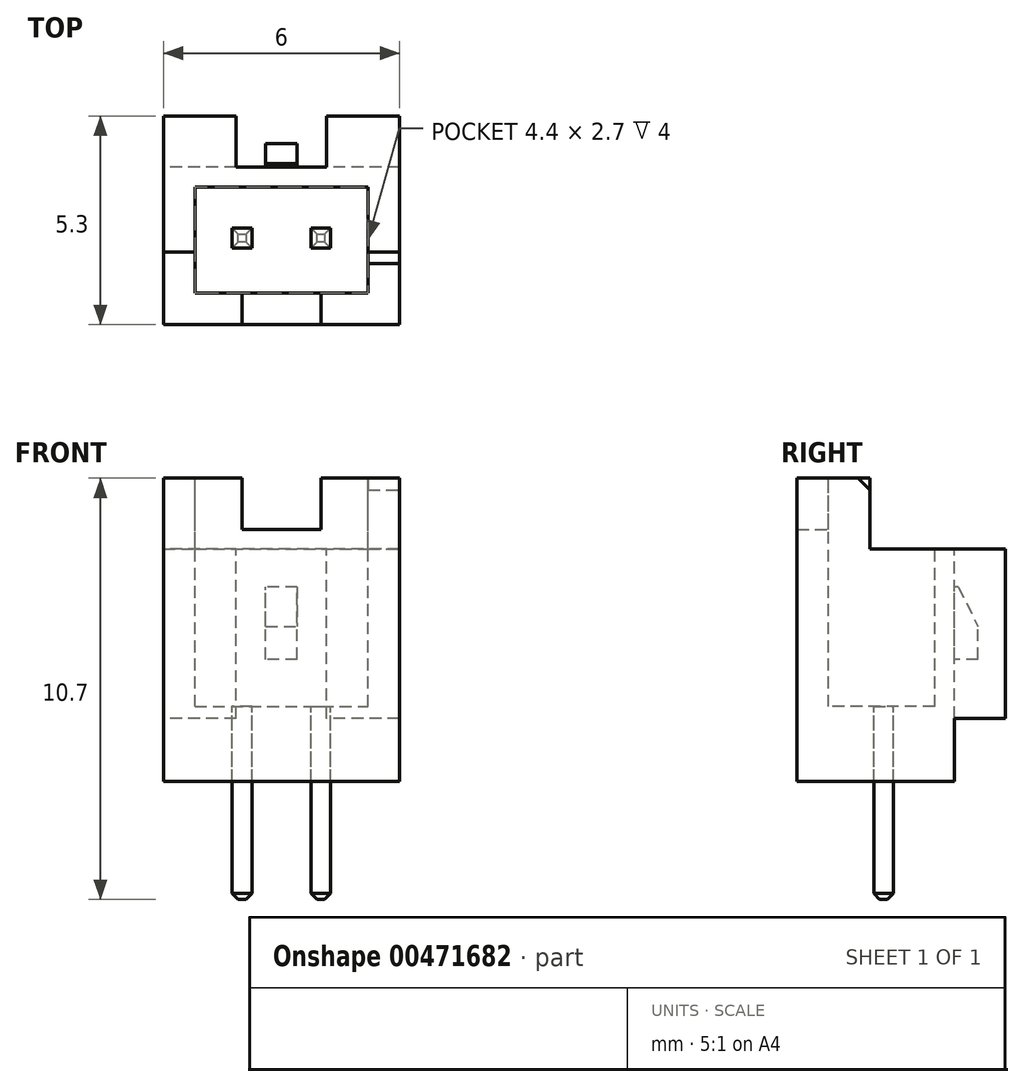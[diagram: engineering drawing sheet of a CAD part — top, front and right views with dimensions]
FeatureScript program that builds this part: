
annotation { "Feature Type Name" : "Feature", "Feature Type Description" : "" }
export const myFeature = defineFeature(function(context is Context, id is Id, definition is map)
    precondition{}
    {
        {
            var Q0;
            Q0=qCreatedBy(makeId("Top.planeOp"),FACE);
            var sketch = newSketch(context, id + "F0", { "sketchPlane" : qUnion([Q0])});
            skLineSegment(sketch, "E0.bottom", {"start": v(0.25, 0.25) * mm, "end": v(-0.25, 0.25) * mm});
            skLineSegment(sketch, "E0.top", {"start": v(0.25, -0.25) * mm, "end": v(-0.25, -0.25) * mm});
            skLineSegment(sketch, "E0.left", {"start": v(0.25, 0.25) * mm, "end": v(0.25, -0.25) * mm});
            skLineSegment(sketch, "E0.right", {"start": v(-0.25, 0.25) * mm, "end": v(-0.25, -0.25) * mm});
            skPoint(sketch, "E0.middle", {"position": v(0, 0) * mm});
            skLineSegment(sketch, "E1.bottom", {"start": v(-2.25, 0.25) * mm, "end": v(-1.75, 0.25) * mm});
            skLineSegment(sketch, "E1.top", {"start": v(-2.25, -0.25) * mm, "end": v(-1.75, -0.25) * mm});
            skLineSegment(sketch, "E1.left", {"start": v(-2.25, 0.25) * mm, "end": v(-2.25, -0.25) * mm});
            skLineSegment(sketch, "E1.right", {"start": v(-1.75, 0.25) * mm, "end": v(-1.75, -0.25) * mm});
            skPoint(sketch, "E1.middle", {"position": v(-2, 0) * mm});
            skSolve(sketch);
        }
        {
            var Q0;
            Q0=makeQuery(id+"F0.imprint","IMPRINT",FACE,{"disambiguationData":[TD([[makeQuery(id+"F0.imprint","IMPRINT",EDGE,{"derivedFrom":sQuery(id+"F0.wireOp",EDGE,"E1.bottom")}),-1.0]])]});
            var Q1;
            Q1=makeQuery(id+"F0.imprint","IMPRINT",FACE,{"disambiguationData":[TD([[makeQuery(id+"F0.imprint","IMPRINT",EDGE,{"derivedFrom":sQuery(id+"F0.wireOp",EDGE,"E0.bottom")}),1.0]])]});
            extrude(context, id + "F1", {"entities" : qUnion([Q0, Q1]), "oppositeDirection" : true, "depth" : 3 * mm, "hasSecondDirection" : true, "secondDirectionOppositeDirection" : false, "secondDirectionDepth" : 4 * mm});
        }
        {
            var Q0;
            Q0=qCreatedBy(makeId("Top.planeOp"),FACE);
            var sketch = newSketch(context, id + "F2", { "sketchPlane" : qUnion([Q0])});
            skLineSegment(sketch, "E2.bottom", {"start": v(2, -2.2) * mm, "end": v(-4, -2.2) * mm});
            skLineSegment(sketch, "E2.top", {"start": v(2, 3.1) * mm, "end": v(-4, 3.1) * mm});
            skLineSegment(sketch, "E2.left", {"start": v(2, -2.2) * mm, "end": v(2, 3.1) * mm});
            skLineSegment(sketch, "E2.right", {"start": v(-4, -2.2) * mm, "end": v(-4, 3.1) * mm});
            skSolve(sketch);
        }
        {
            var Q0;
            Q0=makeQuery(id+"F2.imprint","IMPRINT",FACE,{"disambiguationData":[TD([[makeQuery(id+"F2.imprint","IMPRINT",EDGE,{"derivedFrom":sQuery(id+"F2.wireOp",EDGE,"E2.bottom")}),-1.0]])]});
            extrude(context, id + "F3", {"entities" : qUnion([Q0]), "depth" : 7.7 * mm});
        }
        {
            var Q0;
            Q0=makeQuery(id+"F3.opExtrude","CAP_FACE",FACE,{"disambiguationData":[OSD([sQuery(id+"F2.wireOp",EDGE,"E2.bottom"),sQuery(id+"F2.wireOp",EDGE,"E2.top"),sQuery(id+"F2.wireOp",EDGE,"E2.left"),sQuery(id+"F2.wireOp",EDGE,"E2.right")])],"isStart":false});
            var sketch = newSketch(context, id + "F4", { "sketchPlane" : qUnion([Q0])});
            skLineSegment(sketch, "E3.bottom", {"start": v(-3.2, 1.3) * mm, "end": v(1.2, 1.3) * mm});
            skLineSegment(sketch, "E3.top", {"start": v(-3.2, -1.4) * mm, "end": v(1.2, -1.4) * mm});
            skLineSegment(sketch, "E3.left", {"start": v(-3.2, 1.3) * mm, "end": v(-3.2, -1.4) * mm});
            skLineSegment(sketch, "E3.right", {"start": v(1.2, 1.3) * mm, "end": v(1.2, -1.4) * mm});
            skSolve(sketch);
        }
        {
            var Q0;
            Q0=makeQuery(id+"F4.imprint","IMPRINT",FACE,{"disambiguationData":[TD([[makeQuery(id+"F4.imprint","IMPRINT",EDGE,{"derivedFrom":sQuery(id+"F4.wireOp",EDGE,"E3.bottom")}),-1.0]])]});
            extrude(context, id + "F5", {"entities" : qUnion([Q0]), "operationType" : NewBodyOperationType.REMOVE, "oppositeDirection" : true, "depth" : 5.8 * mm});
        }
        {
            var Q0;
            Q0=makeQuery(id+"F3.opExtrude","CAP_FACE",FACE,{"disambiguationData":[OSD([sQuery(id+"F2.wireOp",EDGE,"E2.bottom"),sQuery(id+"F2.wireOp",EDGE,"E2.top"),sQuery(id+"F2.wireOp",EDGE,"E2.left"),sQuery(id+"F2.wireOp",EDGE,"E2.right")])],"isStart":false});
            var sketch = newSketch(context, id + "F6", { "sketchPlane" : qUnion([Q0])});
            skLineSegment(sketch, "E4.bottom", {"start": v(-2, -2.2) * mm, "end": v(0, -2.2) * mm});
            skLineSegment(sketch, "E4.top", {"start": v(-2, -1.4) * mm, "end": v(0, -1.4) * mm});
            skLineSegment(sketch, "E4.left", {"start": v(-2, -2.2) * mm, "end": v(-2, -1.4) * mm});
            skLineSegment(sketch, "E4.right", {"start": v(0, -2.2) * mm, "end": v(0, -1.4) * mm});
            skLineSegment(sketch, "E5.bottom", {"start": v(-4, 3.1) * mm, "end": v(2, 3.1) * mm});
            skLineSegment(sketch, "E5.top", {"start": v(-4, -0.35) * mm, "end": v(2, -0.35) * mm});
            skLineSegment(sketch, "E5.left", {"start": v(-4, 3.1) * mm, "end": v(-4, -0.35) * mm});
            skLineSegment(sketch, "E5.right", {"start": v(2, 3.1) * mm, "end": v(2, -0.35) * mm});
            skSolve(sketch);
        }
        {
            var Q0;
            Q0=makeQuery(id+"F6.imprint","IMPRINT",FACE,{"disambiguationData":[TD([[makeQuery(id+"F6.imprint","IMPRINT",EDGE,{"derivedFrom":sQuery(id+"F6.wireOp",EDGE,"E4.bottom")}),-1.0]])]});
            extrude(context, id + "F7", {"entities" : qUnion([Q0]), "operationType" : NewBodyOperationType.REMOVE, "oppositeDirection" : true, "depth" : 1.3 * mm});
        }
        {
            var Q0;
            Q0=makeQuery(id+"F6.imprint","IMPRINT",FACE,{"disambiguationData":[TD([[makeQuery(id+"F6.imprint","IMPRINT",EDGE,{"derivedFrom":sQuery(id+"F6.wireOp",EDGE,"E5.bottom")}),1.0]])]});
            extrude(context, id + "F8", {"entities" : qUnion([Q0]), "operationType" : NewBodyOperationType.REMOVE, "oppositeDirection" : true, "depth" : 1.8 * mm});
        }
        {
            var Q0;
            Q0=makeQuery(id+"F8.boolean.opBoolean","COPY",FACE,{"derivedFrom":makeQuery(id+"F8.opExtrude","CAP_FACE",FACE,{"disambiguationData":[OSD([sQuery(id+"F4.wireOp",EDGE,"E3.bottom"),sQuery(id+"F4.wireOp",EDGE,"E3.left"),sQuery(id+"F4.wireOp",EDGE,"E3.right"),sQuery(id+"F6.wireOp",EDGE,"E5.bottom"),sQuery(id+"F6.wireOp",EDGE,"E5.top"),sQuery(id+"F6.wireOp",EDGE,"E5.left"),sQuery(id+"F6.wireOp",EDGE,"E5.right")])],"isStart":false})});
            var sketch = newSketch(context, id + "F9", { "sketchPlane" : qUnion([Q0])});
            skLineSegment(sketch, "E6.bottom", {"start": v(0.15, 3.1) * mm, "end": v(-2.15, 3.1) * mm});
            skLineSegment(sketch, "E6.top", {"start": v(0.15, 1.8) * mm, "end": v(-2.15, 1.8) * mm});
            skLineSegment(sketch, "E6.left", {"start": v(0.15, 3.1) * mm, "end": v(0.15, 1.8) * mm});
            skLineSegment(sketch, "E6.right", {"start": v(-2.15, 3.1) * mm, "end": v(-2.15, 1.8) * mm});
            skSolve(sketch);
        }
        {
            var Q0;
            Q0=makeQuery(id+"F9.imprint","IMPRINT",FACE,{"disambiguationData":[TD([[makeQuery(id+"F9.imprint","IMPRINT",EDGE,{"derivedFrom":sQuery(id+"F9.wireOp",EDGE,"E6.bottom")}),1.0]])]});
            extrude(context, id + "F10", {"entities" : qUnion([Q0]), "operationType" : NewBodyOperationType.REMOVE, "oppositeDirection" : true, "depth" : 25 * mm});
        }
        {
            var Q0;
            Q0=makeQuery(id+"F10.boolean.opBoolean","COPY",FACE,{"derivedFrom":makeQuery(id+"F10.opExtrude","SWEPT_FACE",FACE,{"disambiguationData":[OSD([sQuery(id+"F9.wireOp",EDGE,"E6.top")])]})});
            var sketch = newSketch(context, id + "F11", { "sketchPlane" : qUnion([Q0])});
            skLineSegment(sketch, "E7.bottom", {"start": v(0.6, 3.1) * mm, "end": v(1.4, 3.1) * mm});
            skLineSegment(sketch, "E7.top", {"start": v(0.6, 4.94) * mm, "end": v(1.4, 4.94) * mm});
            skLineSegment(sketch, "E7.left", {"start": v(0.6, 3.1) * mm, "end": v(0.6, 4.94) * mm});
            skLineSegment(sketch, "E7.right", {"start": v(1.4, 3.1) * mm, "end": v(1.4, 4.94) * mm});
            skSolve(sketch);
        }
        {
            var Q0;
            Q0=makeQuery(id+"F11.imprint","IMPRINT",FACE,{"disambiguationData":[TD([[makeQuery(id+"F11.imprint","IMPRINT",EDGE,{"derivedFrom":sQuery(id+"F11.wireOp",EDGE,"E7.bottom")}),1.0]])]});
            extrude(context, id + "F12", {"entities" : qUnion([Q0]), "operationType" : NewBodyOperationType.ADD, "depth" : 0.6 * mm});
        }
        {
            var Q0;
            Q0=makeQuery(id+"F3.opExtrude","CAP_FACE",FACE,{"disambiguationData":[OSD([sQuery(id+"F2.wireOp",EDGE,"E2.bottom"),sQuery(id+"F2.wireOp",EDGE,"E2.top"),sQuery(id+"F2.wireOp",EDGE,"E2.left"),sQuery(id+"F2.wireOp",EDGE,"E2.right")])],"isStart":true});
            var sketch = newSketch(context, id + "F13", { "sketchPlane" : qUnion([Q0])});
            skLineSegment(sketch, "E8.bottom", {"start": v(2, -1.8) * mm, "end": v(-4, -1.8) * mm});
            skLineSegment(sketch, "E8.top", {"start": v(2, -3.1) * mm, "end": v(-4, -3.1) * mm});
            skLineSegment(sketch, "E8.left", {"start": v(2, -1.8) * mm, "end": v(2, -3.1) * mm});
            skLineSegment(sketch, "E8.right", {"start": v(-4, -1.8) * mm, "end": v(-4, -3.1) * mm});
            skSolve(sketch);
        }
        {
            var Q0;
            {var subQ3=sQuery(id+"F13.wireOp",EDGE,"E8.right");Q0=makeQuery(id+"F13.imprint","IMPRINT",FACE,{"disambiguationData":[TD([[makeQuery(id+"F13.imprint","IMPRINT",EDGE,{"derivedFrom":subQ3}),1.0]])]});}
            var Q1;
            {var subQ3=sQuery(id+"F13.wireOp",EDGE,"E8.left");Q1=makeQuery(id+"F13.imprint","IMPRINT",FACE,{"disambiguationData":[TD([[makeQuery(id+"F13.imprint","IMPRINT",EDGE,{"derivedFrom":subQ3}),-1.0]])]});}
            extrude(context, id + "F14", {"entities" : qUnion([Q0, Q1]), "operationType" : NewBodyOperationType.REMOVE, "oppositeDirection" : true, "depth" : 1.6 * mm});
        }
        {
            var Q0;
            Q0=makeQuery(id+"F12.opExtrude","CAP_EDGE",EDGE,{"disambiguationData":[OSD([sQuery(id+"F11.wireOp",EDGE,"E7.top")])],"isStart":false});
            chamfer(context, id + "F15", {"entities" : qUnion([Q0]), "chamferType" : ChamferType.TWO_OFFSETS, "width1" : .5 * mm, "oppositeDirection" : false, "width2" : 1 * mm, "tangentPropagation" : true});
        }
        {
            var Q0;
            {var subQ0=sQuery(id+"F4.wireOp",EDGE,"E3.top");Q0=makeQuery(id+"F7.boolean.opBoolean","SPLIT",EDGE,{"disambiguationData":[TD([makeQuery(id+"F5.boolean.opBoolean","COPY",FACE,{"derivedFrom":makeQuery(id+"F5.opExtrude","SWEPT_FACE",FACE,{"disambiguationData":[OSD([sQuery(id+"F4.wireOp",EDGE,"E3.left")])]})})])],"derivedFrom":makeQuery(id+"F5.boolean.opBoolean","COPY",EDGE,{"derivedFrom":makeQuery(id+"F5.opExtrude","CAP_EDGE",EDGE,{"disambiguationData":[OSD([subQ0])],"isStart":true})})});}
            var Q1;
            Q1=makeQuery(id+"F5.boolean.opBoolean","COPY",EDGE,{"derivedFrom":makeQuery(id+"F5.opExtrude","CAP_EDGE",EDGE,{"disambiguationData":[OSD([sQuery(id+"F4.wireOp",EDGE,"E3.left")])],"isStart":true})});
            var Q2;
            {var subQ0=sQuery(id+"F4.wireOp",EDGE,"E3.top");Q2=makeQuery(id+"F7.boolean.opBoolean","SPLIT",EDGE,{"disambiguationData":[TD([makeQuery(id+"F5.boolean.opBoolean","COPY",FACE,{"derivedFrom":makeQuery(id+"F5.opExtrude","SWEPT_FACE",FACE,{"disambiguationData":[OSD([sQuery(id+"F4.wireOp",EDGE,"E3.right")])]})})])],"derivedFrom":makeQuery(id+"F5.boolean.opBoolean","COPY",EDGE,{"derivedFrom":makeQuery(id+"F5.opExtrude","CAP_EDGE",EDGE,{"disambiguationData":[OSD([subQ0])],"isStart":true})})});}
            var Q3;
            Q3=makeQuery(id+"F5.boolean.opBoolean","COPY",EDGE,{"derivedFrom":makeQuery(id+"F5.opExtrude","CAP_EDGE",EDGE,{"disambiguationData":[OSD([sQuery(id+"F4.wireOp",EDGE,"E3.right")])],"isStart":true})});
            var Q4;
            Q4=makeQuery(id+"F7.boolean.opBoolean","COPY",EDGE,{"derivedFrom":makeQuery(id+"F7.opExtrude","CAP_EDGE",EDGE,{"disambiguationData":[OSD([sQuery(id+"F6.wireOp",EDGE,"E4.left")])],"isStart":true})});
            var Q5;
            Q5=makeQuery(id+"F7.boolean.opBoolean","COPY",EDGE,{"derivedFrom":makeQuery(id+"F7.opExtrude","CAP_EDGE",EDGE,{"disambiguationData":[OSD([sQuery(id+"F6.wireOp",EDGE,"E4.right")])],"isStart":true})});
            var Q6;
            {var subQ0=sQuery(id+"F6.wireOp",EDGE,"E5.top");Q6=makeQuery(id+"F8.boolean.opBoolean","COPY",EDGE,{"derivedFrom":makeQuery(id+"F8.opExtrude","CAP_EDGE",EDGE,{"disambiguationData":[OSD([subQ0]),TDD([makeQuery(id+"F6.imprint","IMPRINT",EDGE,{"disambiguationData":[TD([[makeQuery(id+"F6.imprint","INTERSECT",VERTEX,{"derivedFrom":[makeQuery(id+"F5.boolean.opBoolean","COPY",EDGE,{"derivedFrom":makeQuery(id+"F5.opExtrude","CAP_EDGE",EDGE,{"disambiguationData":[OSD([sQuery(id+"F4.wireOp",EDGE,"E3.left")])],"isStart":true})}),subQ0]}),1.0]])],"derivedFrom":subQ0})])],"isStart":true})});}
            var Q7;
            {var subQ0=sQuery(id+"F6.wireOp",EDGE,"E5.top");Q7=makeQuery(id+"F8.boolean.opBoolean","COPY",EDGE,{"derivedFrom":makeQuery(id+"F8.opExtrude","CAP_EDGE",EDGE,{"disambiguationData":[OSD([subQ0]),TDD([makeQuery(id+"F6.imprint","IMPRINT",EDGE,{"disambiguationData":[TD([[makeQuery(id+"F6.imprint","INTERSECT",VERTEX,{"derivedFrom":[makeQuery(id+"F5.boolean.opBoolean","COPY",EDGE,{"derivedFrom":makeQuery(id+"F5.opExtrude","CAP_EDGE",EDGE,{"disambiguationData":[OSD([sQuery(id+"F4.wireOp",EDGE,"E3.right")])],"isStart":true})}),subQ0]}),-1.0]])],"derivedFrom":subQ0})])],"isStart":true})});}
            var Q8;
            Q8=makeQuery(id+"F8.boolean.opBoolean","COPY",EDGE,{"derivedFrom":makeQuery(id+"F8.opExtrude","SWEPT_EDGE",EDGE,{"disambiguationData":[OSD([sQuery(id+"F4.wireOp",EDGE,"E3.right"),sQuery(id+"F6.wireOp",EDGE,"E5.top")])]})});
            var Q9;
            Q9=makeQuery(id+"F8.boolean.opBoolean","COPY",EDGE,{"derivedFrom":makeQuery(id+"F8.opExtrude","CAP_EDGE",EDGE,{"disambiguationData":[OSD([sQuery(id+"F4.wireOp",EDGE,"E3.right")])],"isStart":false})});
            var Q10;
            Q10=makeQuery(id+"F8.boolean.opBoolean","COPY",EDGE,{"derivedFrom":makeQuery(id+"F8.opExtrude","CAP_EDGE",EDGE,{"disambiguationData":[OSD([sQuery(id+"F4.wireOp",EDGE,"E3.bottom")])],"isStart":false})});
            var Q11;
            Q11=makeQuery(id+"F8.boolean.opBoolean","COPY",EDGE,{"derivedFrom":makeQuery(id+"F8.opExtrude","CAP_EDGE",EDGE,{"disambiguationData":[OSD([sQuery(id+"F4.wireOp",EDGE,"E3.left")])],"isStart":false})});
            var Q12;
            Q12=makeQuery(id+"F8.boolean.opBoolean","COPY",EDGE,{"derivedFrom":makeQuery(id+"F8.opExtrude","SWEPT_EDGE",EDGE,{"disambiguationData":[OSD([sQuery(id+"F4.wireOp",EDGE,"E3.left"),sQuery(id+"F6.wireOp",EDGE,"E5.top")])]})});
            chamfer(context, id + "F16", {"entities" : qUnion([Q0, Q1, Q2, Q3, Q4, Q5, Q6, Q7, Q8, Q9, Q10, Q11, Q12]), "width" : .3 * mm, "tangentPropagation" : true});
        }
        {
            var Q0;
            Q0=makeQuery(id+"F1.opExtrude","CAP_FACE",FACE,{"disambiguationData":[OSD([sQuery(id+"F0.wireOp",EDGE,"E0.bottom"),sQuery(id+"F0.wireOp",EDGE,"E0.top"),sQuery(id+"F0.wireOp",EDGE,"E0.left"),sQuery(id+"F0.wireOp",EDGE,"E0.right")])],"isStart":true});
            var Q1;
            Q1=makeQuery(id+"F1.opExtrude","CAP_FACE",FACE,{"disambiguationData":[OSD([sQuery(id+"F0.wireOp",EDGE,"E1.bottom"),sQuery(id+"F0.wireOp",EDGE,"E1.top"),sQuery(id+"F0.wireOp",EDGE,"E1.left"),sQuery(id+"F0.wireOp",EDGE,"E1.right")])],"isStart":true});
            var Q2;
            Q2=makeQuery(id+"F1.opExtrude","CAP_FACE",FACE,{"disambiguationData":[OSD([sQuery(id+"F0.wireOp",EDGE,"E1.bottom"),sQuery(id+"F0.wireOp",EDGE,"E1.top"),sQuery(id+"F0.wireOp",EDGE,"E1.left"),sQuery(id+"F0.wireOp",EDGE,"E1.right")])],"isStart":false});
            var Q3;
            Q3=makeQuery(id+"F1.opExtrude","CAP_EDGE",EDGE,{"disambiguationData":[OSD([sQuery(id+"F0.wireOp",EDGE,"E0.left")])],"isStart":false});
            var Q4;
            Q4=makeQuery(id+"F1.opExtrude","CAP_FACE",FACE,{"disambiguationData":[OSD([sQuery(id+"F0.wireOp",EDGE,"E0.bottom"),sQuery(id+"F0.wireOp",EDGE,"E0.top"),sQuery(id+"F0.wireOp",EDGE,"E0.left"),sQuery(id+"F0.wireOp",EDGE,"E0.right")])],"isStart":false});
            chamfer(context, id + "F17", {"entities" : qUnion([Q0, Q1, Q2, Q3, Q4]), "width" : 0.15 * mm, "tangentPropagation" : true});
        }
    });
